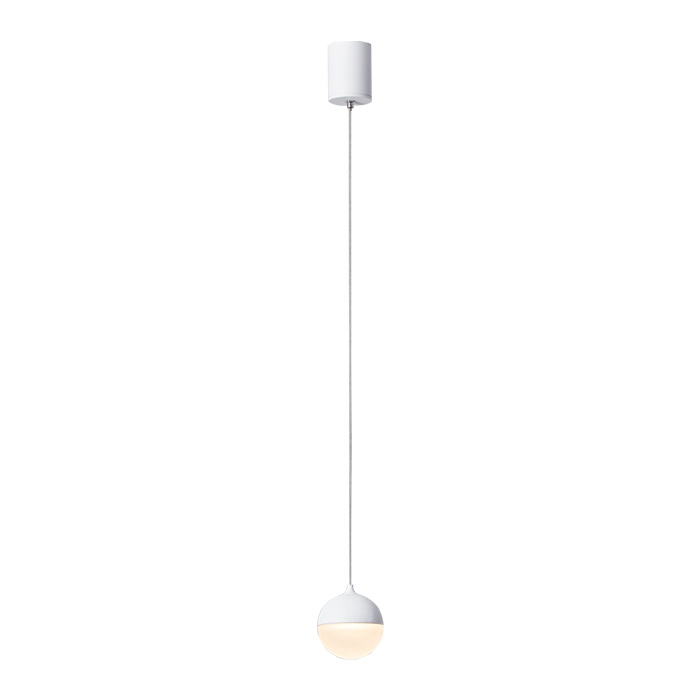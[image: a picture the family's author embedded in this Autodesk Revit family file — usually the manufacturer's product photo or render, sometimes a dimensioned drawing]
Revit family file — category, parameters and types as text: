
# Revit family: Pearl Single 5W
name_source: partatom
category: Lighting Fixtures
revit_build: Autodesk Revit 2017 (Build: 20160225_1515(x64)
units: mm (PartAtom-declared; Revit-internal decimal feet)

## family parameters
Cut with Voids When Loaded = No
Host = Face
Light Source = No
OmniClass Number = 23.80.70.11.11
OmniClass Title = General Luminaries, Non Directional
Part Type = Normal
Room Calculation Point = No
Round Connector Dimension = Use Diameter
Shared = No

## types (2) — shared parameters
CRI = 82
Casing Color = White
Cutout = -
Default Elevation = 1219 mm
Depth = -
Description = Pendant Light
Dimensions = 86mm x 1600mm
Dimmable = Yes
Directivity = No
Driver = Integrated
Housing Material = Aluminium
IP Code = IP20
Lamp = LED
Last Updated = 8.3.2017
Lifetime L70 = 50000h
Manufacturer = Winled Oy Ltd
Operating Temperature Range = -20° to +50°
Type Image = Pearl Single .png
URL = www.winled.fi
Voltage = 230 V
Wattage Comments = 5W

## per-type parameters (varying)
| type | Beam Angle | Color Temperature | Light source | Lumens Output | Model | Product Number |
| Pearl Single 5W, Neutral White, 230V - 53SI995N005J | 160° | 4000K | Pearl light NV | 488lm | Pear Single 5W | 53SI995N005J |
| Pearl Single 5W, Warm White, 230V - 53SI995L005J | 90° | 3000K | Pearl light LV | 388lm | Pearl Single 5W | 53SI995L005J |

## geometry (parser evidence)
native form markers: Sweep x11
no freeform markers — native parametric forms only
